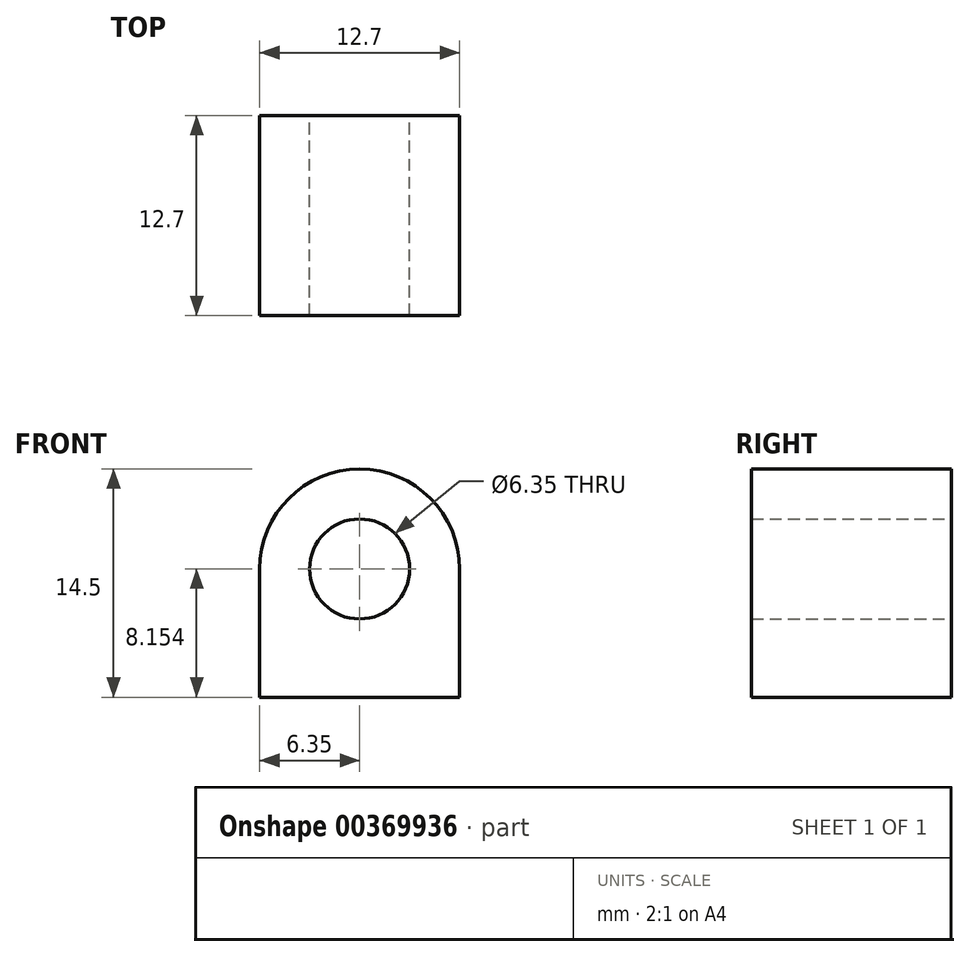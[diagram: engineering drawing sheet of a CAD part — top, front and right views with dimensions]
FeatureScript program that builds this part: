
annotation { "Feature Type Name" : "Feature", "Feature Type Description" : "" }
export const myFeature = defineFeature(function(context is Context, id is Id, definition is map)
    precondition{}
    {
        {
            var Q0;
            Q0=qCreatedBy(makeId("Front.planeOp"),FACE);
            var sketch = newSketch(context, id + "F0", { "sketchPlane" : qUnion([Q0])});
            skLineSegment(sketch, "E0", {"start": v(0, 0) * mm, "end": v(0, 8.15) * mm});
            skLineSegment(sketch, "E1", {"start": v(0, 8.15) * mm, "end": v(12.7, 8.15) * mm});
            skLineSegment(sketch, "E2", {"start": v(12.7, 8.15) * mm, "end": v(12.7, 0) * mm});
            skLineSegment(sketch, "E3", {"start": v(12.7, 0) * mm, "end": v(0, 0) * mm});
            skArc(sketch, "E4", {"start": v(12.7, 8.15) * mm, "mid": v(6.35, 14.5) * mm, "end": v(0, 8.15) * mm});
            skCircle(sketch, "E5", {"center": v(6.35, 8.15) * mm, "radius": 3.18 * mm});
            skSolve(sketch);
        }
        {
            var Q0;
            Q0 = qSketchRegion(id + "F0", true);
            extrude(context, id + "F1", {"entities" : qUnion([Q0]), "depth" : 12.7 * mm});
        }
    });
